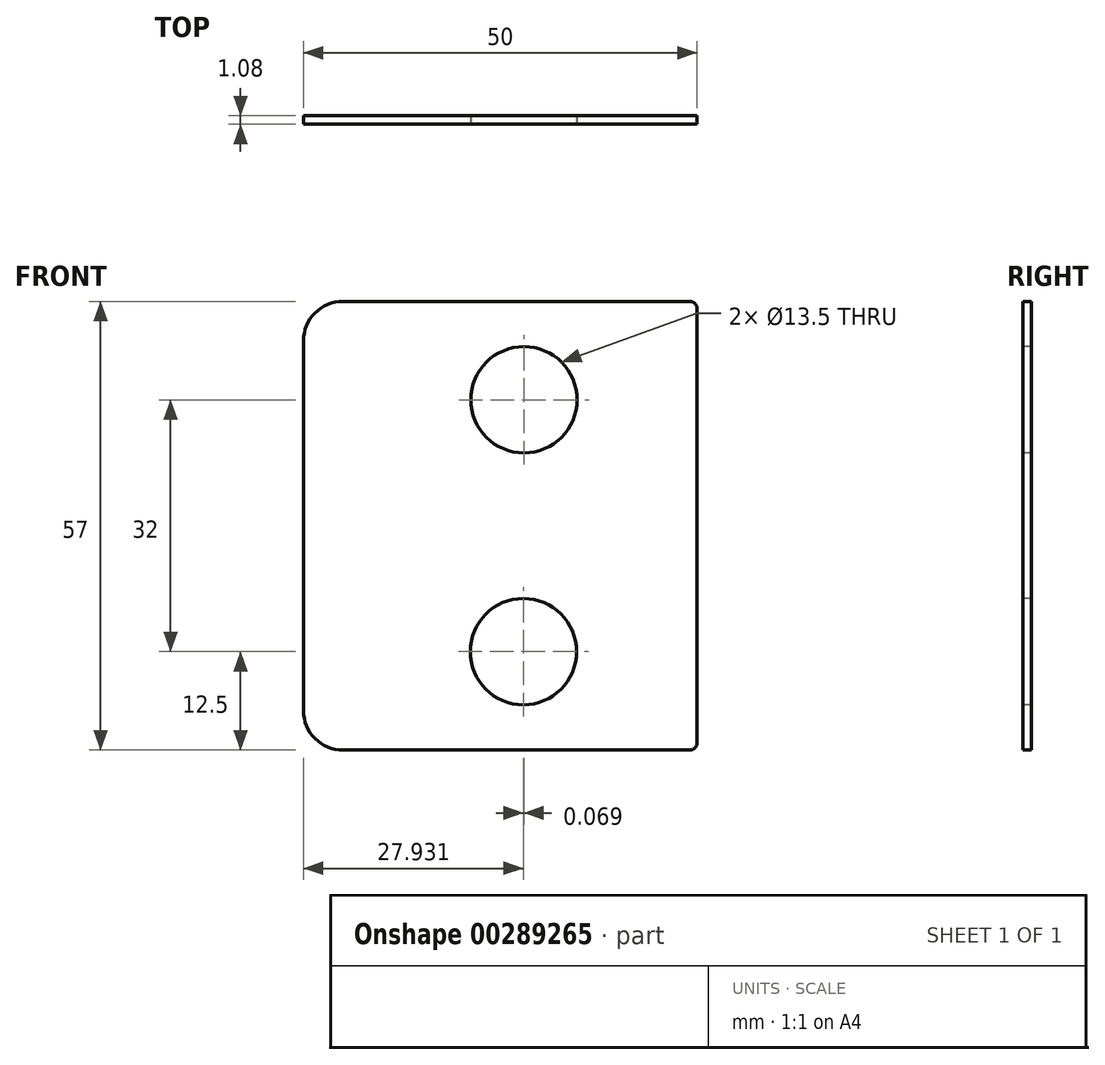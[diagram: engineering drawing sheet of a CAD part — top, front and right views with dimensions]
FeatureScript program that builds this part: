
annotation { "Feature Type Name" : "Feature", "Feature Type Description" : "" }
export const myFeature = defineFeature(function(context is Context, id is Id, definition is map)
    precondition{}
    {
        {
            var Q0;
            Q0=qCreatedBy(makeId("Front.planeOp"),FACE);
            var sketch = newSketch(context, id + "F0", { "sketchPlane" : qUnion([Q0])});
            skLineSegment(sketch, "E0.bottom", {"start": v(-1, 0) * mm, "end": v(-45, 0) * mm});
            skLineSegment(sketch, "E0.top", {"start": v(-1, 57) * mm, "end": v(-45, 57) * mm});
            skLineSegment(sketch, "E0.left", {"start": v(0, 1) * mm, "end": v(0, 56) * mm});
            skLineSegment(sketch, "E0.right", {"start": v(-50, 5) * mm, "end": v(-50, 52) * mm});
            skPoint(sketch, "E1.visualSharp", {"position": v(-50, 57) * mm});
            skArc(sketch, "E1.filletArc", {"start": v(-45, 57) * mm, "mid": v(-48.54, 55.54) * mm, "end": v(-50, 52) * mm});
            skPoint(sketch, "E2.visualSharp", {"position": v(-50, 0) * mm});
            skArc(sketch, "E2.filletArc", {"start": v(-50, 5) * mm, "mid": v(-48.54, 1.46) * mm, "end": v(-45, 0) * mm});
            skPoint(sketch, "E3.visualSharp", {"position": v(0, 0) * mm});
            skArc(sketch, "E3.filletArc", {"start": v(-1, 0) * mm, "mid": v(-0.3, 0.3) * mm, "end": v(0, 1) * mm});
            skPoint(sketch, "E4.visualSharp", {"position": v(0, 57) * mm});
            skArc(sketch, "E4.filletArc", {"start": v(0, 56) * mm, "mid": v(-0.3, 56.7) * mm, "end": v(-1, 57) * mm});
            skSolve(sketch);
        }
        {
            var Q0;
            Q0=makeQuery(id+"F0.imprint","IMPRINT",FACE,{"disambiguationData":[TD([[makeQuery(id+"F0.imprint","IMPRINT",EDGE,{"derivedFrom":sQuery(id+"F0.wireOp",EDGE,"E0.bottom")}),-1.0]])]});
            extrude(context, id + "F1", {"entities" : qUnion([Q0]), "depth" : 1.08 * mm});
        }
        {
            var Q0;
            Q0=makeQuery(id+"F1.opExtrude","CAP_FACE",FACE,{"disambiguationData":[OSD([sQuery(id+"F0.wireOp",EDGE,"E0.bottom"),sQuery(id+"F0.wireOp",EDGE,"E0.top"),sQuery(id+"F0.wireOp",EDGE,"E0.left"),sQuery(id+"F0.wireOp",EDGE,"E0.right"),sQuery(id+"F0.wireOp",EDGE,"E1.filletArc"),sQuery(id+"F0.wireOp",EDGE,"E2.filletArc"),sQuery(id+"F0.wireOp",EDGE,"E3.filletArc"),sQuery(id+"F0.wireOp",EDGE,"E4.filletArc")])],"isStart":false});
            var sketch = newSketch(context, id + "F2", { "sketchPlane" : qUnion([Q0])});
            skCircle(sketch, "E5", {"center": v(-22, 44.5) * mm, "radius": 6.75 * mm});
            skCircle(sketch, "E6", {"center": v(-22.07, 12.5) * mm, "radius": 6.75 * mm});
            skSolve(sketch);
        }
        {
            var Q0;
            Q0=sQuery(id+"F2.wireOp",VERTEX,"E5.center");
            var Q1;
            Q1=sQuery(id+"F2.wireOp",VERTEX,"E6.center");
            var Q2;
            Q2=makeQuery(id+"F1.opExtrude","SWEPT_BODY",BODY,{"disambiguationData":[OSD([sQuery(id+"F0.wireOp",EDGE,"E0.bottom"),sQuery(id+"F0.wireOp",EDGE,"E0.top"),sQuery(id+"F0.wireOp",EDGE,"E0.left"),sQuery(id+"F0.wireOp",EDGE,"E0.right"),sQuery(id+"F0.wireOp",EDGE,"E1.filletArc"),sQuery(id+"F0.wireOp",EDGE,"E2.filletArc"),sQuery(id+"F0.wireOp",EDGE,"E3.filletArc"),sQuery(id+"F0.wireOp",EDGE,"E4.filletArc")])]});
            hole(context, id + "F3", {"style" : HoleStyle.SIMPLE, "endStyle" : HoleEndStyle.THROUGH, "holeDiameter" : 13.5 * mm, "tappedDepth" : 10 * mm, "tapClearance" : 3, "locations" : qUnion([Q0, Q1]), "scope" : qUnion([Q2])});
        }
    });
